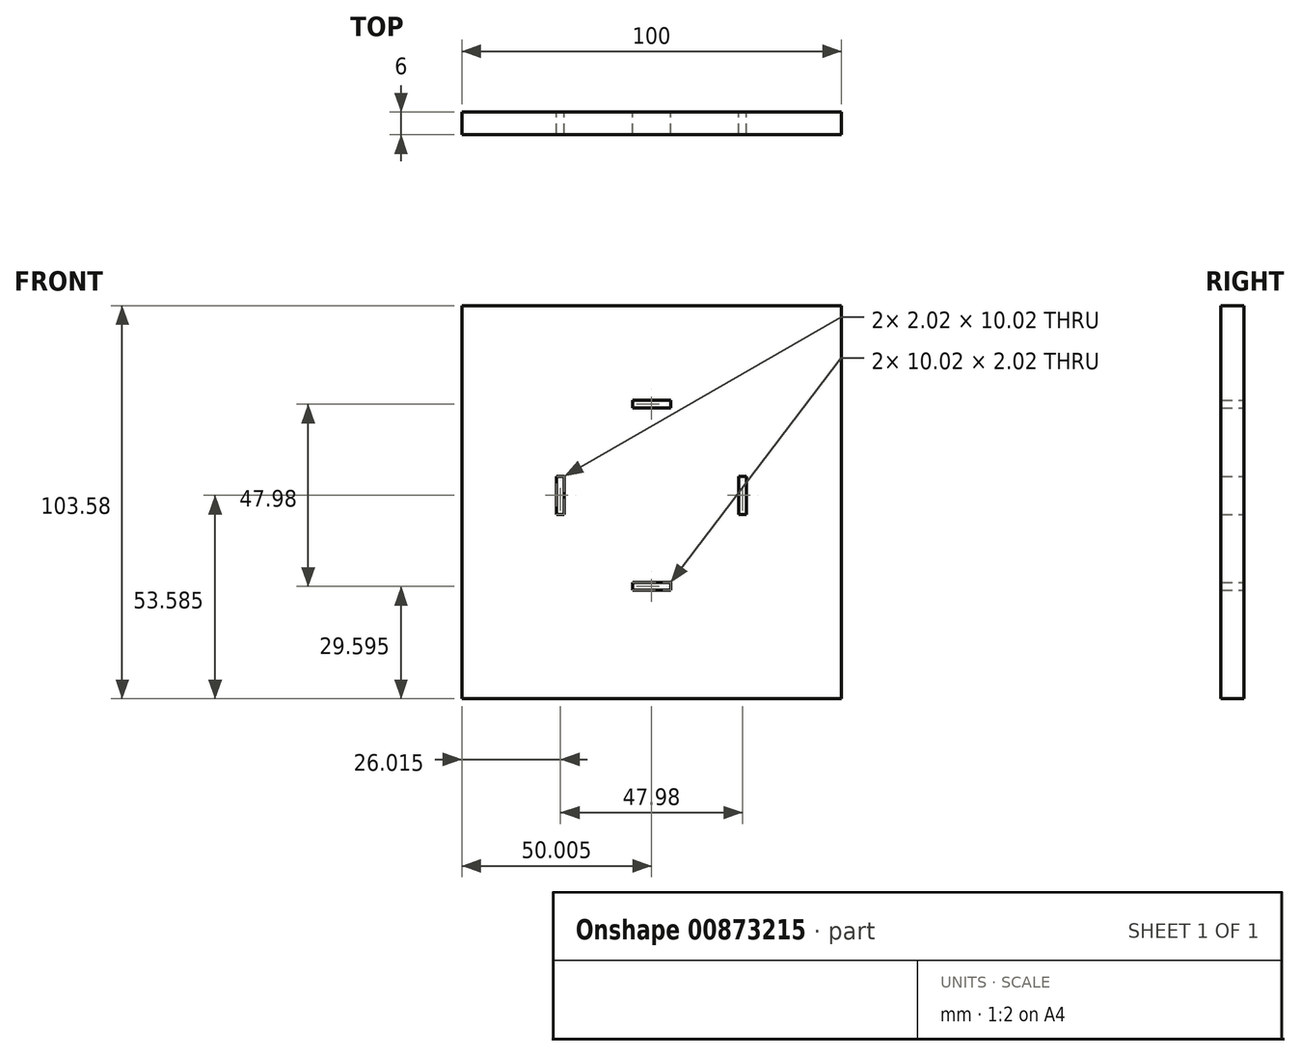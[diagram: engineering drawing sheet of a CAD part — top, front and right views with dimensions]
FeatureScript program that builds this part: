
annotation { "Feature Type Name" : "Feature", "Feature Type Description" : "" }
export const myFeature = defineFeature(function(context is Context, id is Id, definition is map)
    precondition{}
    {
        {
            var Q0;
            Q0=qCreatedBy(makeId("Front.planeOp"),FACE);
            var sketch = newSketch(context, id + "F0", { "sketchPlane" : qUnion([Q0])});
            skLineSegment(sketch, "E0.bottom", {"start": v(-48.38, 47.93) * mm, "end": v(51.62, 47.93) * mm});
            skLineSegment(sketch, "E0.top", {"start": v(-48.38, -55.65) * mm, "end": v(51.62, -55.65) * mm});
            skLineSegment(sketch, "E0.left", {"start": v(-48.38, 47.93) * mm, "end": v(-48.38, -55.65) * mm});
            skLineSegment(sketch, "E0.right", {"start": v(51.62, 47.93) * mm, "end": v(51.62, -55.65) * mm});
            skLineSegment(sketch, "E1.bottom", {"start": v(-23.38, 22.93) * mm, "end": v(26.62, 22.93) * mm, "construction": true});
            skLineSegment(sketch, "E1.top", {"start": v(-23.38, -27.07) * mm, "end": v(26.62, -27.07) * mm, "construction": true});
            skLineSegment(sketch, "E1.left", {"start": v(-23.38, 22.93) * mm, "end": v(-23.38, -27.07) * mm, "construction": true});
            skLineSegment(sketch, "E1.right", {"start": v(26.62, 22.93) * mm, "end": v(26.62, -27.07) * mm, "construction": true});
            skLineSegment(sketch, "E2.bottom", {"start": v(-3.39, 22.93) * mm, "end": v(6.63, 22.93) * mm});
            skLineSegment(sketch, "E2.top", {"start": v(-3.39, 20.91) * mm, "end": v(6.63, 20.91) * mm});
            skLineSegment(sketch, "E2.left", {"start": v(-3.39, 22.93) * mm, "end": v(-3.39, 20.91) * mm});
            skLineSegment(sketch, "E2.right", {"start": v(6.63, 22.93) * mm, "end": v(6.63, 20.91) * mm});
            skLineSegment(sketch, "E3.bottom", {"start": v(26.62, 2.94) * mm, "end": v(24.6, 2.94) * mm});
            skLineSegment(sketch, "E3.top", {"start": v(26.62, -7.08) * mm, "end": v(24.6, -7.08) * mm});
            skLineSegment(sketch, "E3.left", {"start": v(26.62, 2.94) * mm, "end": v(26.62, -7.08) * mm});
            skLineSegment(sketch, "E3.right", {"start": v(24.6, 2.94) * mm, "end": v(24.6, -7.08) * mm});
            skLineSegment(sketch, "E4.bottom", {"start": v(-3.39, -27.07) * mm, "end": v(6.63, -27.07) * mm});
            skLineSegment(sketch, "E4.top", {"start": v(-3.39, -25.05) * mm, "end": v(6.63, -25.05) * mm});
            skLineSegment(sketch, "E4.left", {"start": v(-3.39, -27.07) * mm, "end": v(-3.39, -25.05) * mm});
            skLineSegment(sketch, "E4.right", {"start": v(6.63, -27.07) * mm, "end": v(6.63, -25.05) * mm});
            skLineSegment(sketch, "E5.bottom", {"start": v(-23.38, 2.94) * mm, "end": v(-21.36, 2.94) * mm});
            skLineSegment(sketch, "E5.top", {"start": v(-23.38, -7.08) * mm, "end": v(-21.36, -7.08) * mm});
            skLineSegment(sketch, "E5.left", {"start": v(-23.38, 2.94) * mm, "end": v(-23.38, -7.08) * mm});
            skLineSegment(sketch, "E5.right", {"start": v(-21.36, 2.94) * mm, "end": v(-21.36, -7.08) * mm});
            skSolve(sketch);
        }
        {
            var Q0;
            Q0 = qSketchRegion(id + "F0", true);
            extrude(context, id + "F1", {"entities" : qUnion([Q0]), "depth" : 6 * mm, "offsetDistance" : 25 * mm});
        }
    });
